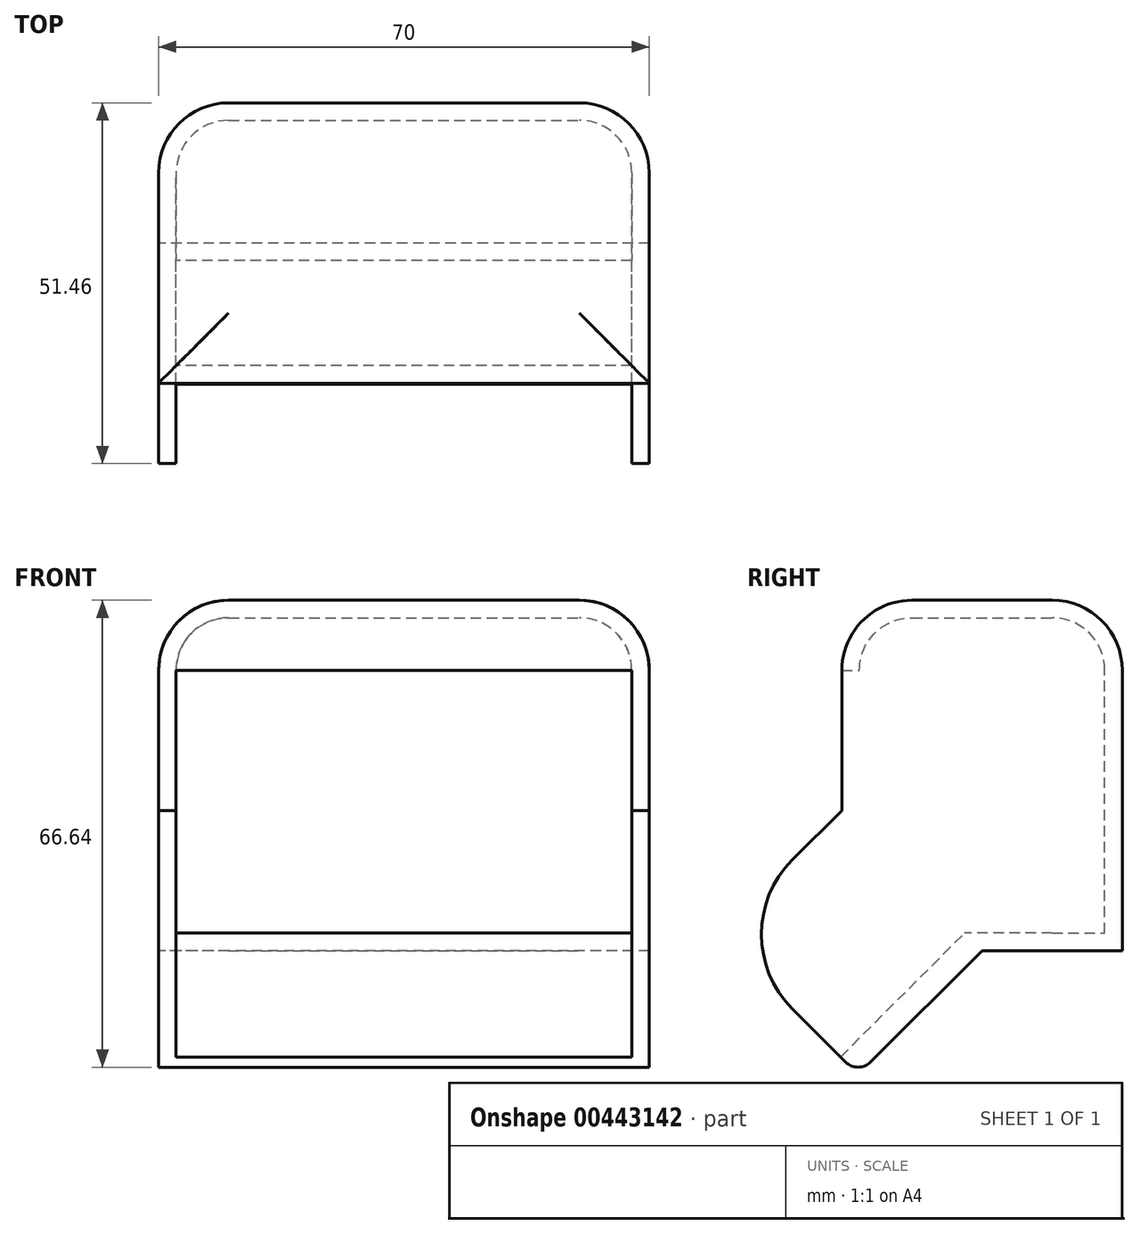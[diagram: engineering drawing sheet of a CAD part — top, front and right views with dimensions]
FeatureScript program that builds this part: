
annotation { "Feature Type Name" : "Feature", "Feature Type Description" : "" }
export const myFeature = defineFeature(function(context is Context, id is Id, definition is map)
    precondition{}
    {
        {
            var Q0;
            Q0=qCreatedBy(makeId("Top.planeOp"),FACE);
            var sketch = newSketch(context, id + "F0", { "sketchPlane" : qUnion([Q0])});
            skLineSegment(sketch, "E0.bottom", {"start": v(-67.44, 1.9) * mm, "end": v(2.56, 1.9) * mm});
            skLineSegment(sketch, "E0.top", {"start": v(-67.44, -38.1) * mm, "end": v(2.56, -38.1) * mm});
            skLineSegment(sketch, "E0.left", {"start": v(-67.44, 1.9) * mm, "end": v(-67.44, -38.1) * mm});
            skLineSegment(sketch, "E0.right", {"start": v(2.56, 1.9) * mm, "end": v(2.56, -38.1) * mm});
            skSolve(sketch);
        }
        {
            var Q0;
            Q0 = qSketchRegion(id + "F0", true);
            extrude(context, id + "F1", {"entities" : qUnion([Q0]), "depth" : 50 * mm});
        }
        {
            var Q0;
            Q0=makeQuery(id+"F1.opExtrude","CAP_EDGE",EDGE,{"disambiguationData":[OSD([sQuery(id+"F0.wireOp",EDGE,"E0.left")])],"isStart":false});
            var Q1;
            Q1=makeQuery(id+"F1.opExtrude","CAP_EDGE",EDGE,{"disambiguationData":[OSD([sQuery(id+"F0.wireOp",EDGE,"E0.top")])],"isStart":false});
            var Q2;
            Q2=makeQuery(id+"F1.opExtrude","CAP_EDGE",EDGE,{"disambiguationData":[OSD([sQuery(id+"F0.wireOp",EDGE,"E0.right")])],"isStart":false});
            var Q3;
            Q3=makeQuery(id+"F1.opExtrude","CAP_EDGE",EDGE,{"disambiguationData":[OSD([sQuery(id+"F0.wireOp",EDGE,"E0.bottom")])],"isStart":false});
            var Q4;
            Q4=makeQuery(id+"F1.opExtrude","SWEPT_EDGE",EDGE,{"disambiguationData":[OSD([sQuery(id+"F0.wireOp",EDGE,"E0.bottom"),sQuery(id+"F0.wireOp",EDGE,"E0.right")])]});
            var Q5;
            Q5=makeQuery(id+"F1.opExtrude","SWEPT_EDGE",EDGE,{"disambiguationData":[OSD([sQuery(id+"F0.wireOp",EDGE,"E0.bottom"),sQuery(id+"F0.wireOp",EDGE,"E0.left")])]});
            fillet(context, id + "F2", {"entities" : qUnion([Q0, Q1, Q2, Q3, Q4, Q5]), "radius" : 10 * mm, "tangentPropagation" : true, "allowEdgeOverflow" : false});
        }
        {
            var Q0;
            Q0=makeQuery(id+"F1.opExtrude","SWEPT_FACE",FACE,{"disambiguationData":[OSD([sQuery(id+"F0.wireOp",EDGE,"E0.top")])]});
            shell(context, id + "F3", {"entities" : qUnion([Q0]), "thickness" : 2.5 * mm});
        }
        {
            var Q0;
            Q0=makeQuery(id+"F1.opExtrude","CAP_EDGE",EDGE,{"disambiguationData":[OSD([sQuery(id+"F0.wireOp",EDGE,"E0.top")])],"isStart":true});
            chamfer(context, id + "F4", {"entities" : qUnion([Q0]), "width" : 20 * mm, "tangentPropagation" : true});
        }
        {
            var Q0;
            Q0=makeQuery(id+"F4.opChamfer","BLEND_FACE",FACE,{"disambiguationData":[OSD([sQuery(id+"F0.wireOp",EDGE,"E0.top")])]});
            extrude(context, id + "F5", {"entities" : qUnion([Q0]), "operationType" : NewBodyOperationType.ADD, "depth" : 25 * mm});
        }
        {
            var Q0;
            {var subQ0=sQuery(id+"F0.wireOp",EDGE,"E0.right");var subQ1=sQuery(id+"F0.wireOp",EDGE,"E0.left");var subQ2=sQuery(id+"F0.wireOp",EDGE,"E0.top");var subQ3=sQuery(id+"F0.wireOp",EDGE,"E0.bottom");Q0=makeQuery(id+"F5.opExtrude","CAP_EDGE",EDGE,{"disambiguationData":[OSD([subQ3,subQ2,subQ1,subQ0]),TDD([makeQuery(id+"F4.opChamfer","BLEND_EDGE",EDGE,{"blendedFrom":[makeQuery(id+"F1.opExtrude","CAP_EDGE",EDGE,{"disambiguationData":[OSD([subQ2])],"isStart":true}),makeQuery(id+"F1.opExtrude","CAP_FACE",FACE,{"disambiguationData":[OSD([subQ3,subQ2,subQ1,subQ0])],"isStart":true})],"blendedInto":[makeQuery(id+"F1.opExtrude","CAP_FACE",FACE,{"disambiguationData":[OSD([subQ3,subQ2,subQ1,subQ0])],"isStart":true})]})])],"isStart":false});}
            fillet(context, id + "F6", {"entities" : qUnion([Q0]), "radius" : 2.5 * mm, "tangentPropagation" : true, "allowEdgeOverflow" : false});
        }
        {
            var Q0;
            {var subQ0=sQuery(id+"F0.wireOp",EDGE,"E0.top");Q0=makeQuery(id+"F5.opExtrude","CAP_EDGE",EDGE,{"disambiguationData":[OSD([subQ0]),TDD([makeQuery(id+"F4.opChamfer","BLEND_EDGE",EDGE,{"disambiguationData":[OD(1.0)],"blendedFrom":[makeQuery(id+"F1.opExtrude","CAP_EDGE",EDGE,{"disambiguationData":[OSD([subQ0])],"isStart":true}),makeQuery(id+"F1.opExtrude","SWEPT_FACE",FACE,{"disambiguationData":[OSD([subQ0])]})],"blendedInto":[makeQuery(id+"F1.opExtrude","SWEPT_FACE",FACE,{"disambiguationData":[OSD([subQ0])]})]})])],"isStart":false});}
            var Q1;
            {var subQ0=sQuery(id+"F0.wireOp",EDGE,"E0.top");Q1=makeQuery(id+"F5.opExtrude","CAP_EDGE",EDGE,{"disambiguationData":[OSD([subQ0]),TDD([makeQuery(id+"F4.opChamfer","BLEND_EDGE",EDGE,{"disambiguationData":[OD(0.0)],"blendedFrom":[makeQuery(id+"F1.opExtrude","CAP_EDGE",EDGE,{"disambiguationData":[OSD([subQ0])],"isStart":true}),makeQuery(id+"F1.opExtrude","SWEPT_FACE",FACE,{"disambiguationData":[OSD([subQ0])]})],"blendedInto":[makeQuery(id+"F1.opExtrude","SWEPT_FACE",FACE,{"disambiguationData":[OSD([subQ0])]})]})])],"isStart":false});}
            fillet(context, id + "F7", {"entities" : qUnion([Q0, Q1]), "radius" : 15 * mm, "tangentPropagation" : true, "allowEdgeOverflow" : false});
        }
    });
